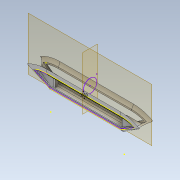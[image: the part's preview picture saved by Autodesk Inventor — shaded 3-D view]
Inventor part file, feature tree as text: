
AUTODESK INVENTOR PART (.ipt)
format: ipt  version: 2021 (Build 250183000, 183)  size: 604,672 bytes
history: native  units: in
note: dims shown in document units (in); Inventor stores cm internally (conversion verified against a paired STEP export)
features: sketch x11, extrude x7, plane x3, fillet x3, sweep x2, mirror x2, move_body x2, direct_edit x1, shell x1, projected_geometry x1
ambient origin geometry x8: Origin, YZ Plane, XZ Plane, XY Plane, X Axis, Y Axis, Z Axis, Center Point
bodies: Solid1 (feature_tree)
feature tree (33):
  extrude  "Extrusion1"  Depth=1.0in
  sweep  "Sweep1"
  direct_edit  "Direct Edit1"
  plane  "Work Plane1"
  plane  "Work Plane2"
  sweep  "Sweep2"
  fillet  "Fillet1"  [1 undecoded]
  fillet  "Fillet2"  Radius=2.75in
  fillet  "Fillet3"  [1 undecoded]
  shell  "Shell1"  Thickness=0.19in
  sketch  "Sketch4"  dims[d10=0.0in d11=0.0in d12=0.375in]
  extrude  "Extrusion2"  Depth=0.05in
  extrude  "Extrusion3"  Depth=0.7068in TaperAngle=0.0deg
  plane  "Work Plane3"
  extrude  "Extrusion5"  Depth=0.7068in
  mirror  "Mirror2"
  extrude  "Extrusion6"  Depth=0.7068in
  extrude  "Extrusion7"  Depth=0.7068in TaperAngle=0.0deg
  extrude  "Extrusion8"  Depth=0.31in TaperAngle=0.0deg
  mirror  "Mirror3"
  sketch  "Sketch10"  dims[d35=0.05in d36=0.0in d37=0.05in d38=0.0in d42=0.5in d43=0.05in d44=0.08in d45=0.0in d46=0.31in d47=0.0in d48=0.12in d49=0.7068in d50=0.0in d51=0.12in d52=0.035in d53=0.035in d54=0.7068in d55=0.0in]
  sketch  "Sketch1"  dims[d0=5.5in d1=1.0in]
  sketch  "Sketch2"  dims[d3=1.0in d4=1.0in]
  sketch  "3D Sketch1"
  sketch  "Sketch3"  dims[d5=1.0in d6=0.0in d7=0.5in d8=0.0in d9=0.0in]
  sketch  "3D Sketch2"
  sketch  "Sketch6"  dims[d13=0.0in d14=0.0in d15=0.375in d16=2.75in d17=0.5in d18=0.0in d19=0.0in]
  projected_geometry  "Projected Loop2"
  sketch  "Sketch7"  dims[d20=0.2in d21=0.2in d22=0.2in d23=0.03in d24=0.03in d25=0.2in]
  sketch  "Sketch8"  dims[d26=0.2in d27=0.2in d28=0.2in d29=0.03in d30=0.03in d31=0.2in d32=0.19in]
  sketch  "Sketch9"  dims[d33=0.1in d34=0.05in]
  move_body  "Move1"
  move_body  "Move2"
note: 2 required parameter values undecoded (feature->parameter linkage not recoverable at this tier; creation-order binding heuristic only, values carry confidence <= 0.55)
